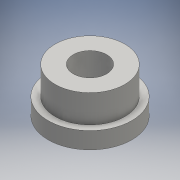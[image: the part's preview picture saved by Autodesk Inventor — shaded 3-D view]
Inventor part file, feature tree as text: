
AUTODESK INVENTOR PART (.ipt)
format: ipt  version: 2016 (Build 200138000, 138)  size: 107,520 bytes
history: native  units: mm
features: extrude x2, sketch x2, other x1
ambient origin geometry x8: Origin, YZ Plane, XZ Plane, XY Plane, X Axis, Y Axis, Z Axis, Center Point
bodies: Body1 (feature_tree)
feature tree (5):
  other  "ソリッド1"
  extrude  "押し出し1"  Depth=12.0mm
  extrude  "押し出し2"  Depth=30.0mm
  sketch  "スケッチ1"
  sketch  "スケッチ2"
